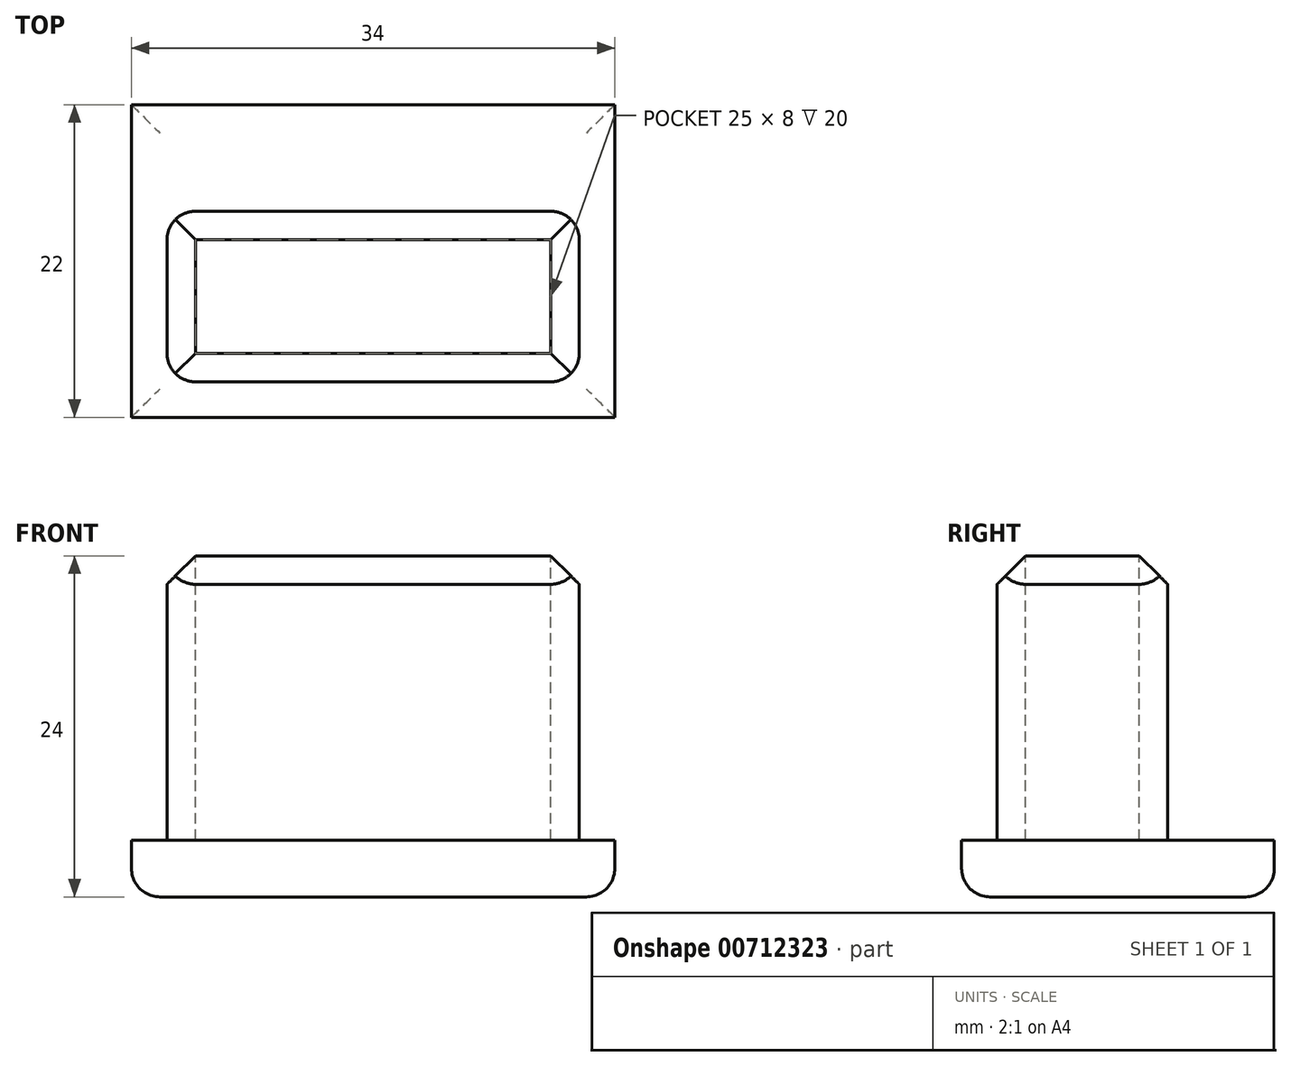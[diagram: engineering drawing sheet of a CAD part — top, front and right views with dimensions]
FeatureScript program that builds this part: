
annotation { "Feature Type Name" : "Feature", "Feature Type Description" : "" }
export const myFeature = defineFeature(function(context is Context, id is Id, definition is map)
    precondition{}
    {
        {
            var Q0;
            Q0=qCreatedBy(makeId("Top.planeOp"),FACE);
            var sketch = newSketch(context, id + "F0", { "sketchPlane" : qUnion([Q0])});
            skLineSegment(sketch, "E0.bottom", {"start": v(17, 11) * mm, "end": v(-17, 11) * mm});
            skLineSegment(sketch, "E0.top", {"start": v(17, -11) * mm, "end": v(-17, -11) * mm});
            skLineSegment(sketch, "E0.left", {"start": v(17, 11) * mm, "end": v(17, -11) * mm});
            skLineSegment(sketch, "E0.right", {"start": v(-17, 11) * mm, "end": v(-17, -11) * mm});
            skPoint(sketch, "E0.middle", {"position": v(0, 0) * mm});
            skSolve(sketch);
        }
        {
            var Q0;
            Q0=makeQuery(id+"F0.imprint","IMPRINT",FACE,{"disambiguationData":[TD([[makeQuery(id+"F0.imprint","IMPRINT",EDGE,{"derivedFrom":sQuery(id+"F0.wireOp",EDGE,"E0.bottom")}),1.0]])]});
            extrude(context, id + "F1", {"entities" : qUnion([Q0]), "depth" : 4 * mm, "offsetDistance" : 25 * mm});
        }
        {
            var Q0;
            Q0=makeQuery(id+"F1.opExtrude","CAP_FACE",FACE,{"disambiguationData":[OSD([sQuery(id+"F0.wireOp",EDGE,"E0.bottom"),sQuery(id+"F0.wireOp",EDGE,"E0.top"),sQuery(id+"F0.wireOp",EDGE,"E0.left"),sQuery(id+"F0.wireOp",EDGE,"E0.right")])],"isStart":false});
            var sketch = newSketch(context, id + "F2", { "sketchPlane" : qUnion([Q0])});
            skLineSegment(sketch, "E1.bottom", {"start": v(-14.5, -8.5) * mm, "end": v(14.5, -8.5) * mm});
            skLineSegment(sketch, "E1.top", {"start": v(-14.5, 3.5) * mm, "end": v(14.5, 3.5) * mm});
            skLineSegment(sketch, "E1.left", {"start": v(-14.5, -8.5) * mm, "end": v(-14.5, 3.5) * mm});
            skLineSegment(sketch, "E1.right", {"start": v(14.5, -8.5) * mm, "end": v(14.5, 3.5) * mm});
            skSolve(sketch);
        }
        {
            var Q0;
            Q0=makeQuery(id+"F2.imprint","IMPRINT",FACE,{"disambiguationData":[TD([[makeQuery(id+"F2.imprint","IMPRINT",EDGE,{"derivedFrom":sQuery(id+"F2.wireOp",EDGE,"E1.bottom")}),1.0]])]});
            extrude(context, id + "F3", {"entities" : qUnion([Q0]), "operationType" : NewBodyOperationType.ADD, "depth" : 20 * mm, "offsetDistance" : 25 * mm});
        }
        {
            var Q0;
            Q0=makeQuery(id+"F3.opExtrude","CAP_EDGE",EDGE,{"disambiguationData":[OSD([sQuery(id+"F2.wireOp",EDGE,"E1.top")])],"isStart":false});
            var Q1;
            Q1=makeQuery(id+"F3.opExtrude","CAP_EDGE",EDGE,{"disambiguationData":[OSD([sQuery(id+"F2.wireOp",EDGE,"E1.left")])],"isStart":false});
            var Q2;
            Q2=makeQuery(id+"F3.opExtrude","CAP_EDGE",EDGE,{"disambiguationData":[OSD([sQuery(id+"F2.wireOp",EDGE,"E1.bottom")])],"isStart":false});
            var Q3;
            Q3=makeQuery(id+"F3.opExtrude","CAP_EDGE",EDGE,{"disambiguationData":[OSD([sQuery(id+"F2.wireOp",EDGE,"E1.right")])],"isStart":false});
            chamfer(context, id + "F4", {"entities" : qUnion([Q0, Q1, Q2, Q3]), "width" : 2 * mm, "tangentPropagation" : true});
        }
        {
            var Q0;
            Q0=makeQuery(id+"F3.opExtrude","CAP_FACE",FACE,{"disambiguationData":[OSD([sQuery(id+"F2.wireOp",EDGE,"E1.bottom"),sQuery(id+"F2.wireOp",EDGE,"E1.top"),sQuery(id+"F2.wireOp",EDGE,"E1.left"),sQuery(id+"F2.wireOp",EDGE,"E1.right")])],"isStart":false});
            extrude(context, id + "F5", {"entities" : qUnion([Q0]), "operationType" : NewBodyOperationType.REMOVE, "oppositeDirection" : true, "depth" : 20 * mm, "offsetDistance" : 25 * mm});
        }
        {
            var Q0;
            Q0=makeQuery(id+"F1.opExtrude","CAP_EDGE",EDGE,{"disambiguationData":[OSD([sQuery(id+"F0.wireOp",EDGE,"E0.top")])],"isStart":true});
            var Q1;
            Q1=makeQuery(id+"F1.opExtrude","CAP_EDGE",EDGE,{"disambiguationData":[OSD([sQuery(id+"F0.wireOp",EDGE,"E0.left")])],"isStart":true});
            var Q2;
            Q2=makeQuery(id+"F1.opExtrude","CAP_EDGE",EDGE,{"disambiguationData":[OSD([sQuery(id+"F0.wireOp",EDGE,"E0.right")])],"isStart":true});
            var Q3;
            Q3=makeQuery(id+"F1.opExtrude","CAP_EDGE",EDGE,{"disambiguationData":[OSD([sQuery(id+"F0.wireOp",EDGE,"E0.bottom")])],"isStart":true});
            fillet(context, id + "F6", {"entities" : qUnion([Q0, Q1, Q2, Q3]), "radius" : 2 * mm, "tangentPropagation" : true, "allowEdgeOverflow" : false});
        }
        {
            var Q0;
            Q0=makeQuery(id+"F3.opExtrude","SWEPT_EDGE",EDGE,{"disambiguationData":[OSD([sQuery(id+"F2.wireOp",EDGE,"E1.bottom"),sQuery(id+"F2.wireOp",EDGE,"E1.left")])]});
            var Q1;
            Q1=makeQuery(id+"F3.opExtrude","SWEPT_EDGE",EDGE,{"disambiguationData":[OSD([sQuery(id+"F2.wireOp",EDGE,"E1.top"),sQuery(id+"F2.wireOp",EDGE,"E1.left")])]});
            var Q2;
            Q2=makeQuery(id+"F3.opExtrude","SWEPT_EDGE",EDGE,{"disambiguationData":[OSD([sQuery(id+"F2.wireOp",EDGE,"E1.bottom"),sQuery(id+"F2.wireOp",EDGE,"E1.right")])]});
            var Q3;
            Q3=makeQuery(id+"F3.opExtrude","SWEPT_EDGE",EDGE,{"disambiguationData":[OSD([sQuery(id+"F2.wireOp",EDGE,"E1.top"),sQuery(id+"F2.wireOp",EDGE,"E1.right")])]});
            fillet(context, id + "F7", {"entities" : qUnion([Q0, Q1, Q2, Q3]), "radius" : 2 * mm, "tangentPropagation" : true, "allowEdgeOverflow" : false});
        }
    });
